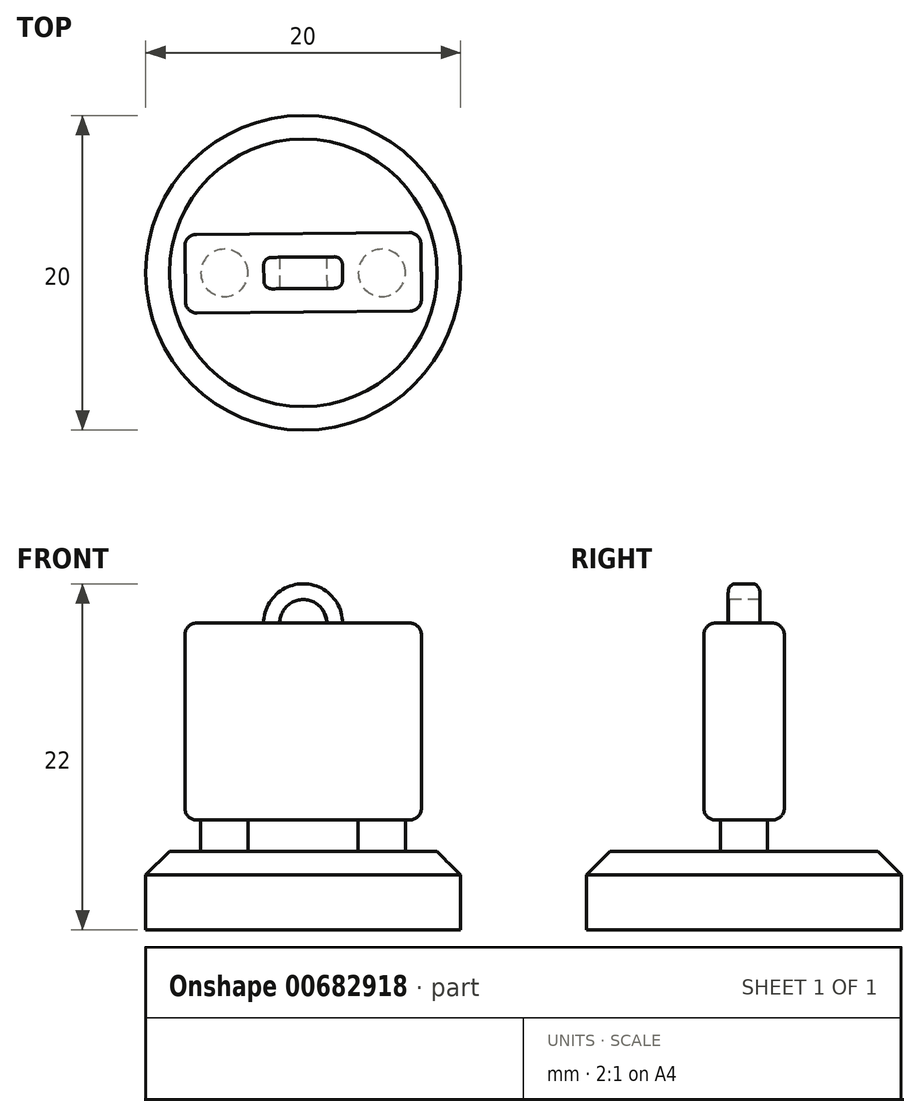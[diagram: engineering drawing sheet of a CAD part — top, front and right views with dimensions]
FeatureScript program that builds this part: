
annotation { "Feature Type Name" : "Feature", "Feature Type Description" : "" }
export const myFeature = defineFeature(function(context is Context, id is Id, definition is map)
    precondition{}
    {
        {
            var Q0;
            Q0=qCreatedBy(makeId("Top.planeOp"),FACE);
            var sketch = newSketch(context, id + "F0", { "sketchPlane" : qUnion([Q0])});
            skCircle(sketch, "E0", {"center": v(0, 0) * mm, "radius": 10 * mm});
            skSolve(sketch);
        }
        {
            var Q0;
            Q0=makeQuery(id+"F0.imprint","IMPRINT",FACE,{"disambiguationData":[TD([[makeQuery(id+"F0.imprint","IMPRINT",EDGE,{"derivedFrom":sQuery(id+"F0.wireOp",EDGE,"E0")}),1.0]])]});
            extrude(context, id + "F1", {"entities" : qUnion([Q0]), "depth" : 5 * mm, "offsetDistance" : 25 * mm});
        }
        {
            var Q0;
            Q0=makeQuery(id+"F1.opExtrude","CAP_EDGE",EDGE,{"disambiguationData":[OSD([sQuery(id+"F0.wireOp",EDGE,"E0")])],"isStart":false});
            chamfer(context, id + "F2", {"entities" : qUnion([Q0]), "width" : 1.5 * mm, "tangentPropagation" : true});
        }
        {
            var Q0;
            Q0=makeQuery(id+"F1.opExtrude","CAP_FACE",FACE,{"disambiguationData":[OSD([sQuery(id+"F0.wireOp",EDGE,"E0")])],"isStart":false});
            var sketch = newSketch(context, id + "F3", { "sketchPlane" : qUnion([Q0])});
            skLineSegment(sketch, "E1", {"start": v(0, 0) * mm, "end": v(-7.5, 0) * mm, "construction": true});
            skLineSegment(sketch, "E2", {"start": v(0, 0) * mm, "end": v(7.5, 0) * mm, "construction": true});
            skLineSegment(sketch, "E3", {"start": v(-7.5, 0) * mm, "end": v(-6.5, 0) * mm, "construction": true});
            skLineSegment(sketch, "E4", {"start": v(7.5, 0) * mm, "end": v(6.5, 0) * mm, "construction": true});
            skLineSegment(sketch, "E5", {"start": v(-6.5, 0) * mm, "end": v(-5, 0) * mm, "construction": true});
            skCircle(sketch, "E6", {"center": v(-5, 0) * mm, "radius": 1.5 * mm});
            skLineSegment(sketch, "E7", {"start": v(6.5, 0) * mm, "end": v(5, 0) * mm, "construction": true});
            skCircle(sketch, "E8", {"center": v(5, 0) * mm, "radius": 1.5 * mm});
            skSolve(sketch);
        }
        {
            var Q0;
            Q0=makeQuery(id+"F3.imprint","IMPRINT",FACE,{"disambiguationData":[TD([[makeQuery(id+"F3.imprint","IMPRINT",EDGE,{"derivedFrom":sQuery(id+"F3.wireOp",EDGE,"E6")}),1.0]])]});
            var Q1;
            Q1=makeQuery(id+"F3.imprint","IMPRINT",FACE,{"disambiguationData":[TD([[makeQuery(id+"F3.imprint","IMPRINT",EDGE,{"derivedFrom":sQuery(id+"F3.wireOp",EDGE,"E8")}),1.0]])]});
            extrude(context, id + "F4", {"entities" : qUnion([Q0, Q1]), "operationType" : NewBodyOperationType.ADD, "depth" : 2 * mm, "offsetDistance" : 25 * mm});
        }
        {
            var Q0;
            Q0=makeQuery(id+"F4.opExtrude","CAP_FACE",FACE,{"disambiguationData":[OSD([sQuery(id+"F3.wireOp",EDGE,"E6")])],"isStart":false});
            var sketch = newSketch(context, id + "F5", { "sketchPlane" : qUnion([Q0])});
            skLineSegment(sketch, "E9", {"start": v(0, 0) * mm, "end": v(-7.5, -0.06) * mm});
            skLineSegment(sketch, "E10", {"start": v(0, 0) * mm, "end": v(7.5, 0) * mm});
            skLineSegment(sketch, "E11", {"start": v(-7.5, -0.06) * mm, "end": v(-7.52, 2.43) * mm});
            skLineSegment(sketch, "E12", {"start": v(-7.5, -0.06) * mm, "end": v(-7.48, -2.56) * mm});
            skLineSegment(sketch, "E13", {"start": v(-7.52, 2.43) * mm, "end": v(7.48, 2.56) * mm});
            skLineSegment(sketch, "E14", {"start": v(-7.48, -2.56) * mm, "end": v(7.52, -2.43) * mm});
            skLineSegment(sketch, "E15", {"start": v(7.52, -2.43) * mm, "end": v(7.48, 2.56) * mm});
            skSolve(sketch);
        }
        {
            var Q0;
            {var subQ0=sQuery(id+"F5.wireOp",EDGE,"E9");var subQ1=makeQuery(id+"F4.opExtrude","CAP_EDGE",EDGE,{"disambiguationData":[OSD([sQuery(id+"F3.wireOp",EDGE,"E6")])],"isStart":false});var subQ2=makeQuery(id+"F5.imprint","INTERSECT",VERTEX,{"disambiguationData":[OD(0.0)],"derivedFrom":[subQ1,subQ0]});Q0=makeQuery(id+"F5.imprint","IMPRINT",FACE,{"disambiguationData":[TD([[makeQuery(id+"F5.imprint","IMPRINT",EDGE,{"disambiguationData":[TD([[subQ2,1.0]])],"derivedFrom":subQ0}),1.0]])]});}
            var Q1;
            {var subQ0=sQuery(id+"F5.wireOp",EDGE,"E9");var subQ1=makeQuery(id+"F4.opExtrude","CAP_EDGE",EDGE,{"disambiguationData":[OSD([sQuery(id+"F3.wireOp",EDGE,"E6")])],"isStart":false});var subQ2=makeQuery(id+"F5.imprint","INTERSECT",VERTEX,{"disambiguationData":[OD(0.0)],"derivedFrom":[subQ1,subQ0]});Q1=makeQuery(id+"F5.imprint","IMPRINT",FACE,{"disambiguationData":[TD([[makeQuery(id+"F5.imprint","IMPRINT",EDGE,{"disambiguationData":[TD([[subQ2,1.0]])],"derivedFrom":subQ0}),-1.0]])]});}
            var Q2;
            Q2=makeQuery(id+"F5.imprint","IMPRINT",FACE,{"disambiguationData":[TD([[makeQuery(id+"F5.imprint","IMPRINT",EDGE,{"derivedFrom":sQuery(id+"F5.wireOp",EDGE,"E11")}),-1.0]])]});
            extrude(context, id + "F6", {"entities" : qUnion([Q0, Q1, Q2]), "operationType" : NewBodyOperationType.ADD, "depth" : 12.5 * mm, "offsetDistance" : 25 * mm});
        }
        {
            var Q0;
            Q0=makeQuery(id+"F6.opExtrude","CAP_EDGE",EDGE,{"disambiguationData":[OSD([sQuery(id+"F5.wireOp",EDGE,"E14")])],"isStart":true});
            var Q1;
            Q1=makeQuery(id+"F6.opExtrude","SWEPT_EDGE",EDGE,{"disambiguationData":[OSD([sQuery(id+"F5.wireOp",EDGE,"E14"),sQuery(id+"F5.wireOp",EDGE,"E15")])]});
            var Q2;
            Q2=makeQuery(id+"F6.opExtrude","SWEPT_EDGE",EDGE,{"disambiguationData":[OSD([sQuery(id+"F5.wireOp",EDGE,"E12"),sQuery(id+"F5.wireOp",EDGE,"E14")])]});
            var Q3;
            Q3=makeQuery(id+"F6.opExtrude","SWEPT_FACE",FACE,{"disambiguationData":[OSD([sQuery(id+"F5.wireOp",EDGE,"E11"),sQuery(id+"F5.wireOp",EDGE,"E12")])]});
            var Q4;
            Q4=makeQuery(id+"F6.opExtrude","CAP_FACE",FACE,{"disambiguationData":[OSD([sQuery(id+"F5.wireOp",EDGE,"E11"),sQuery(id+"F5.wireOp",EDGE,"E12"),sQuery(id+"F5.wireOp",EDGE,"E13"),sQuery(id+"F5.wireOp",EDGE,"E14"),sQuery(id+"F5.wireOp",EDGE,"E15")])],"isStart":false});
            var Q5;
            Q5=makeQuery(id+"F6.opExtrude","SWEPT_FACE",FACE,{"disambiguationData":[OSD([sQuery(id+"F5.wireOp",EDGE,"E15")])]});
            var Q6;
            Q6=makeQuery(id+"F6.opExtrude","SWEPT_FACE",FACE,{"disambiguationData":[OSD([sQuery(id+"F5.wireOp",EDGE,"E13")])]});
            fillet(context, id + "F7", {"entities" : qUnion([Q0, Q1, Q2, Q3, Q4, Q5, Q6]), "radius" : .75 * mm, "tangentPropagation" : true, "allowEdgeOverflow" : false});
        }
        {
            var Q0;
            Q0=makeQuery(id+"F6.opExtrude","SWEPT_FACE",FACE,{"disambiguationData":[OSD([sQuery(id+"F5.wireOp",EDGE,"E13")])]});
            cPlane(context, id + "F8", {"entities" : qUnion([Q0]), "cplaneType" : CPlaneType.OFFSET, "offset" : 2.5 * mm, "oppositeDirection" : true, "width" : 150 * mm, "height" : 150 * mm});
        }
        {
            var Q0;
            Q0=qCreatedBy(id+"F8.planeOp",FACE);
            var sketch = newSketch(context, id + "F9", { "sketchPlane" : qUnion([Q0])});
            skLineSegment(sketch, "E16", {"start": v(0, 0) * mm, "end": v(0, 19.5) * mm, "construction": true});
            skLineSegment(sketch, "E17", {"start": v(0, 19.5) * mm, "end": v(2.5, 19.5) * mm});
            skArc(sketch, "E18", {"start": v(2.5, 19.5) * mm, "mid": v(0, 22) * mm, "end": v(-2.5, 19.5) * mm});
            skArc(sketch, "E19.0", {"start": v(1.5, 19.5) * mm, "mid": v(0, 21) * mm, "end": v(-1.5, 19.5) * mm});
            skLineSegment(sketch, "E20", {"start": v(-1.5, 19.5) * mm, "end": v(-2.5, 19.5) * mm});
            skSolve(sketch);
        }
        {
            var Q0;
            {var subQ0=sQuery(id+"F9.wireOp",EDGE,"E18");Q0=makeQuery(id+"F9.imprint","IMPRINT",FACE,{"disambiguationData":[TD([[makeQuery(id+"F9.imprint","IMPRINT",EDGE,{"derivedFrom":subQ0}),1.0]])]});}
            extrude(context, id + "F10", {"entities" : qUnion([Q0]), "operationType" : NewBodyOperationType.ADD, "depth" : 1 * mm, "offsetDistance" : 25 * mm});
        }
        {
            var Q0;
            Q0=makeQuery(id+"F10.opExtrude","CAP_FACE",FACE,{"disambiguationData":[OSD([sQuery(id+"F9.wireOp",EDGE,"E17"),sQuery(id+"F9.wireOp",EDGE,"E18"),sQuery(id+"F9.wireOp",EDGE,"E19.0"),sQuery(id+"F9.wireOp",EDGE,"E20")])],"isStart":true});
            extrude(context, id + "F11", {"entities" : qUnion([Q0]), "operationType" : NewBodyOperationType.ADD, "depth" : 1 * mm, "offsetDistance" : 25 * mm});
        }
        {
            var Q0;
            Q0=makeQuery(id+"F10.opExtrude","CAP_EDGE",EDGE,{"disambiguationData":[OSD([sQuery(id+"F9.wireOp",EDGE,"E18")])],"isStart":false});
            var Q1;
            Q1=makeQuery(id+"F11.opExtrude","CAP_EDGE",EDGE,{"disambiguationData":[OSD([sQuery(id+"F9.wireOp",EDGE,"E18")])],"isStart":false});
            fillet(context, id + "F12", {"entities" : qUnion([Q0, Q1]), "radius" : .5 * mm, "tangentPropagation" : true, "allowEdgeOverflow" : false});
        }
    });
